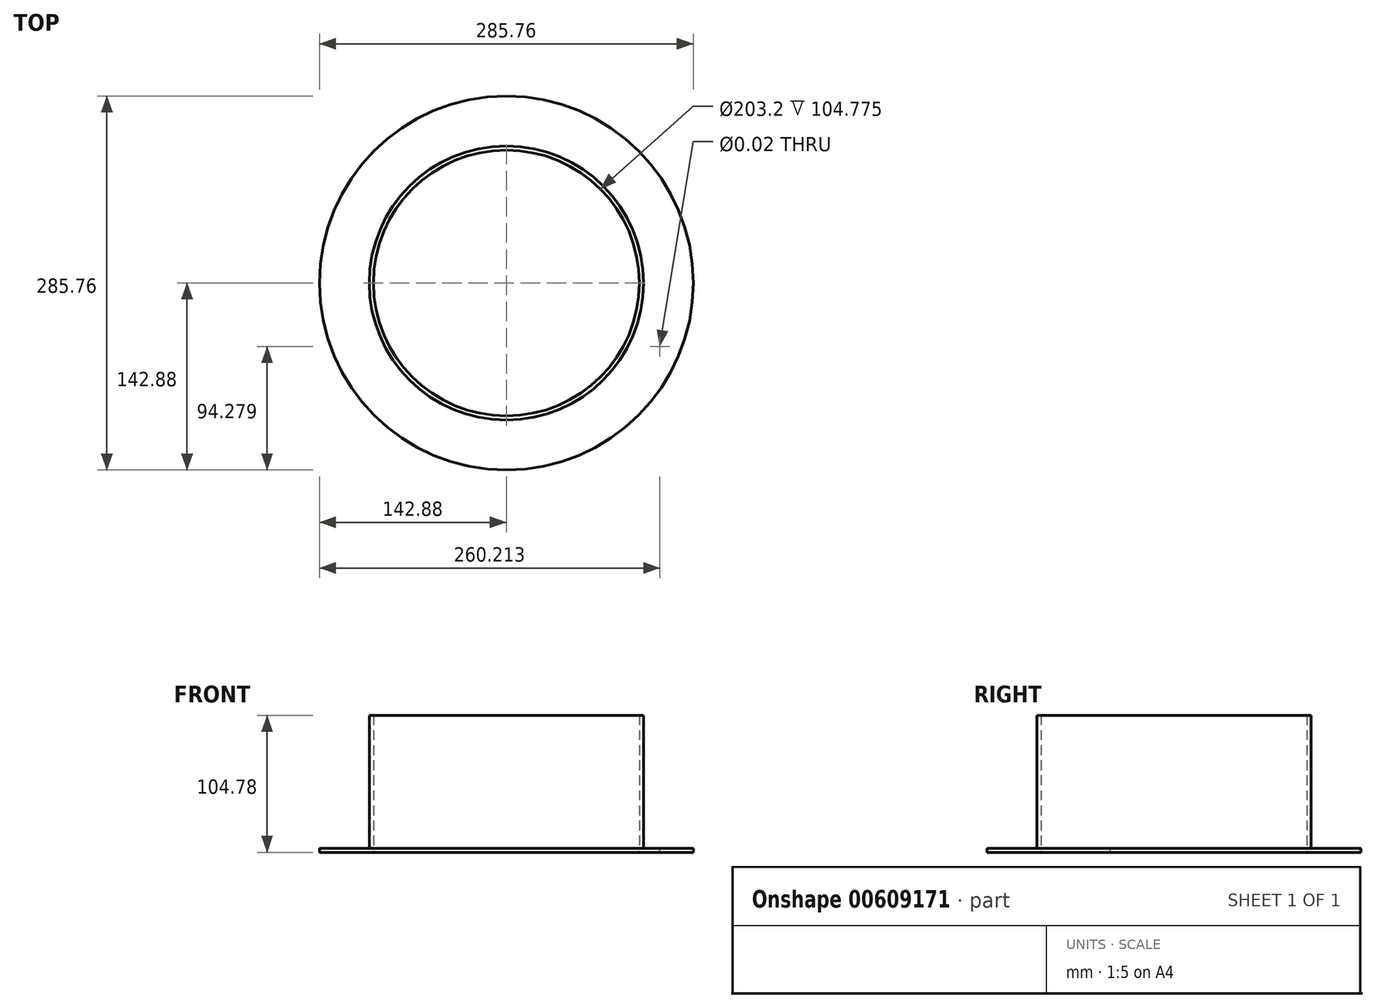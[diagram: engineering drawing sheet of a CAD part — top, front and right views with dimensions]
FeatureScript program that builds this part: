
annotation { "Feature Type Name" : "Feature", "Feature Type Description" : "" }
export const myFeature = defineFeature(function(context is Context, id is Id, definition is map)
    precondition{}
    {
        {
            var Q0;
            Q0=qCreatedBy(makeId("Top.planeOp"),FACE);
            var sketch = newSketch(context, id + "F0", { "sketchPlane" : qUnion([Q0])});
            skCircle(sketch, "E0", {"center": v(0, 0) * mm, "radius": 101.6 * mm});
            skCircle(sketch, "E1", {"center": v(0, 0) * mm, "radius": 104.78 * mm});
            skSolve(sketch);
        }
        {
            var Q0;
            Q0 = qSketchRegion(id + "F0", true);
            extrude(context, id + "F1", {"entities" : qUnion([Q0]), "depth" : 101.6 * mm, "offsetDistance" : 25.4 * mm});
        }
        {
            var Q0;
            Q0=makeQuery(id+"F1.opExtrude","CAP_FACE",FACE,{"disambiguationData":[OSD([sQuery(id+"F0.wireOp",EDGE,"E0"),sQuery(id+"F0.wireOp",EDGE,"E1")])],"isStart":true});
            var sketch = newSketch(context, id + "F2", { "sketchPlane" : qUnion([Q0])});
            skCircle(sketch, "E2", {"center": v(0, 0) * mm, "radius": 142.88 * mm});
            skCircle(sketch, "E3.0", {"center": v(0, 0) * mm, "radius": 101.6 * mm});
            skSolve(sketch);
        }
        {
            var Q0;
            Q0 = qSketchRegion(id + "F2", true);
            extrude(context, id + "F3", {"entities" : qUnion([Q0]), "operationType" : NewBodyOperationType.ADD, "depth" : 3.17 * mm, "offsetDistance" : 25.4 * mm});
        }
        {
            var Q0;
            Q0=makeQuery(id+"F3.opExtrude","CAP_FACE",FACE,{"disambiguationData":[OSD([sQuery(id+"F2.wireOp",EDGE,"E2"),sQuery(id+"F2.wireOp",EDGE,"E3.0")])],"isStart":true});
            var sketch = newSketch(context, id + "F4", { "sketchPlane" : qUnion([Q0])});
            skLineSegment(sketch, "E4", {"start": v(0, 0) * mm, "end": v(142.88, 0) * mm, "construction": true});
            skLineSegment(sketch, "E5", {"start": v(0, 0) * mm, "end": v(117.33, -48.6) * mm, "construction": true});
            skSolve(sketch);
        }
        {
            var Q0;
            Q0=sQuery(id+"F4.wireOp",VERTEX,"E5.end");
            var Q1;
            Q1=makeQuery(id+"F1.opExtrude","SWEPT_BODY",BODY,{"disambiguationData":[OSD([sQuery(id+"F0.wireOp",EDGE,"E0"),sQuery(id+"F0.wireOp",EDGE,"E1")])]});
            hole(context, id + "F5", {"style" : HoleStyle.SIMPLE, "endStyle" : HoleEndStyle.THROUGH, "standardTappedOrClearance" : lookupTablePath({ "standard" : "ANSI", "size" : "25/64 (0.4)", "type" : "Drilled" }), "standardBlindInLast" : lookupTablePath({ "standard" : "ANSI", "size" : "25/64", "type" : "Drilled" }), "holeDiameter" : 25 / 1625.6 * mm, "majorDiameter" : 6.35 * mm, "isTappedThrough" : true, "tappedDepth" : 12.7 * mm, "tapClearance" : 3, "locations" : qUnion([Q0]), "scope" : qUnion([Q1])});
        }
    });
